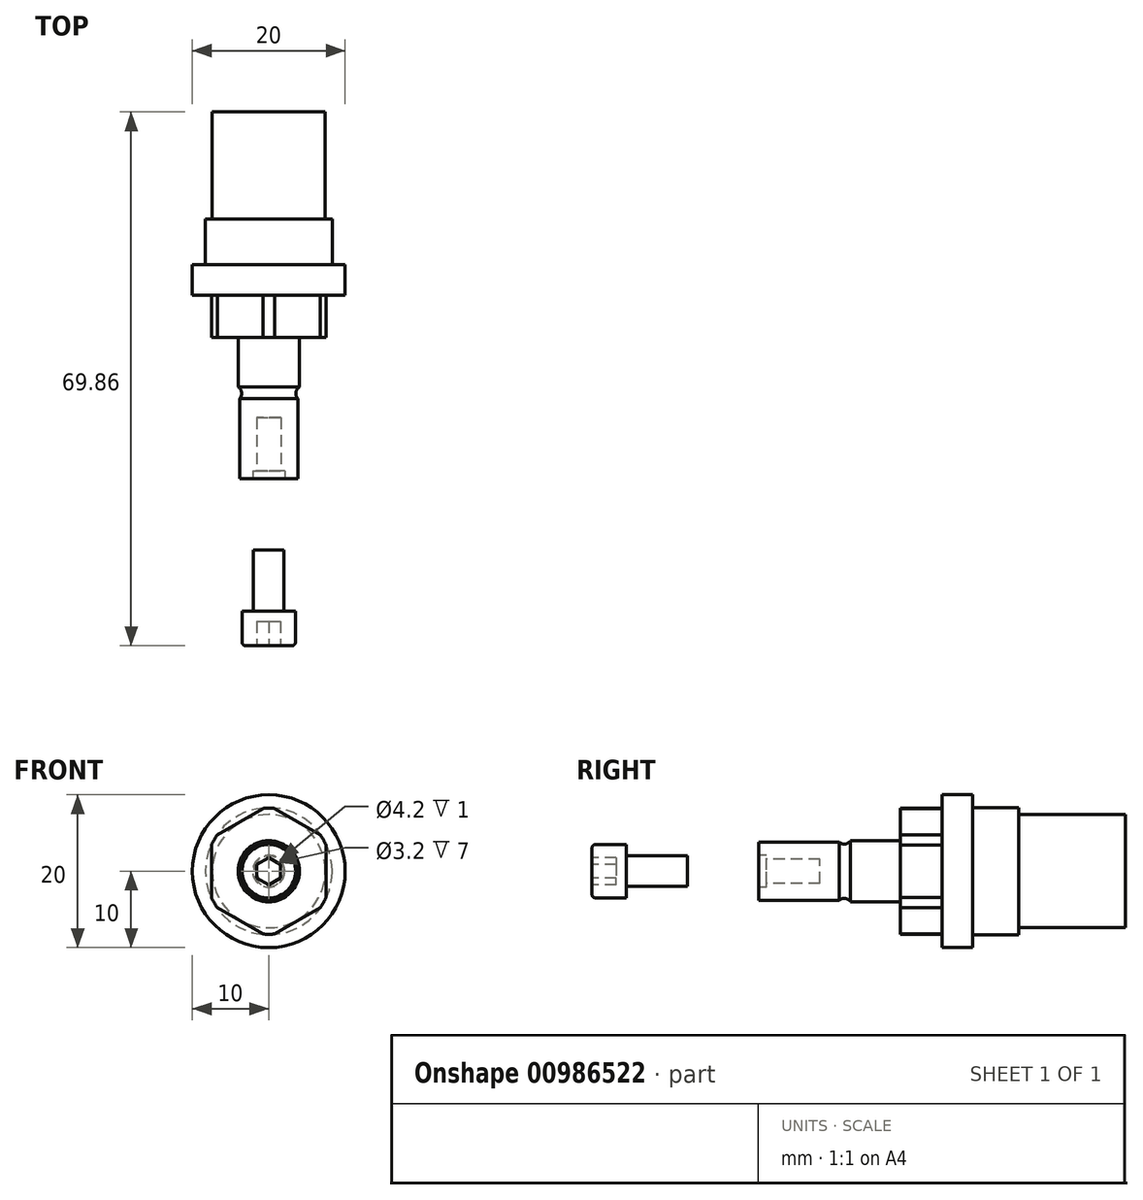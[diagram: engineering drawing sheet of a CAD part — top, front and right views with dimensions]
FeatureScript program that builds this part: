
annotation { "Feature Type Name" : "Feature", "Feature Type Description" : "" }
export const myFeature = defineFeature(function(context is Context, id is Id, definition is map)
    precondition{}
    {
        {
            var Q0;
            Q0=qCreatedBy(makeId("Right.planeOp"),FACE);
            var sketch = newSketch(context, id + "F0", { "sketchPlane" : qUnion([Q0])});
            skLineSegment(sketch, "E0", {"start": v(-42.4, 0) * mm, "end": v(45.83, 0) * mm, "construction": true});
            skLineSegment(sketch, "E1", {"start": v(20, 0) * mm, "end": v(20, 7.4) * mm});
            skLineSegment(sketch, "E2", {"start": v(20, 7.4) * mm, "end": v(6, 7.4) * mm});
            skLineSegment(sketch, "E3", {"start": v(6, 7.4) * mm, "end": v(6, 8.3) * mm});
            skLineSegment(sketch, "E4", {"start": v(6, 8.3) * mm, "end": v(0, 8.3) * mm});
            skLineSegment(sketch, "E5", {"start": v(0, 8.3) * mm, "end": v(0, 10) * mm});
            skLineSegment(sketch, "E6", {"start": v(0, 10) * mm, "end": v(-4, 10) * mm});
            skLineSegment(sketch, "E7", {"start": v(-4, 10) * mm, "end": v(-4, 8.25) * mm});
            skLineSegment(sketch, "E8", {"start": v(-4, 8.25) * mm, "end": v(-9.5, 8.25) * mm});
            skLineSegment(sketch, "E9", {"start": v(-9.5, 8.25) * mm, "end": v(-9.5, 4) * mm});
            skLineSegment(sketch, "E10", {"start": v(-9.5, 4) * mm, "end": v(-16, 4) * mm});
            skLineSegment(sketch, "E11", {"start": v(-17.5, 3.8) * mm, "end": v(-28, 3.8) * mm});
            skLineSegment(sketch, "E12", {"start": v(-28, 3.8) * mm, "end": v(-28, 2.1) * mm});
            skLineSegment(sketch, "E13", {"start": v(-28, 0) * mm, "end": v(20, 0) * mm});
            skArc(sketch, "E14", {"start": v(-17.5, 3.8) * mm, "mid": v(-16.7, 3.56) * mm, "end": v(-16, 4) * mm});
            skLineSegment(sketch, "E15", {"start": v(-28, 2.1) * mm, "end": v(-27, 2.1) * mm});
            skLineSegment(sketch, "E16", {"start": v(-27, 2.1) * mm, "end": v(-27, 1.6) * mm});
            skLineSegment(sketch, "E17", {"start": v(-27, 1.6) * mm, "end": v(-20, 1.6) * mm});
            skLineSegment(sketch, "E18", {"start": v(-20, 1.6) * mm, "end": v(-20, 0) * mm});
            skSolve(sketch);
        }
        {
            var Q0;
            Q0 = qSketchRegion(id + "F0", true);
            var Q1;
            Q1=sQuery(id+"F0.wireOp",EDGE,"E0");
            revolve(context, id + "F1", {"surfaceOperationType" : NewSurfaceOperationType.NEW, "entities" : qUnion([Q0]), "axis" : qUnion([Q1]), "revolveType" : RevolveType.FULL});
        }
        {
            var Q0;
            Q0=makeQuery(id+"F1.opRevolve","SWEPT_FACE",FACE,{"disambiguationData":[OSD([sQuery(id+"F0.wireOp",EDGE,"E9")])]});
            var sketch = newSketch(context, id + "F2", { "sketchPlane" : qUnion([Q0])});
            skCircle(sketch, "E19.cCircle", {"center": v(0, 0) * mm, "radius": 7.5 * mm, "construction": true});
            skLineSegment(sketch, "E19.0", {"start": v(7.5, 4.33) * mm, "end": v(7.5, -4.33) * mm});
            skLineSegment(sketch, "E19.1", {"start": v(7.5, -4.33) * mm, "end": v(0, -8.66) * mm});
            skLineSegment(sketch, "E19.2", {"start": v(0, -8.66) * mm, "end": v(-7.5, -4.33) * mm});
            skLineSegment(sketch, "E19.3", {"start": v(-7.5, -4.33) * mm, "end": v(-7.5, 4.33) * mm});
            skLineSegment(sketch, "E19.4", {"start": v(-7.5, 4.33) * mm, "end": v(0, 8.66) * mm});
            skLineSegment(sketch, "E19.5", {"start": v(0, 8.66) * mm, "end": v(7.5, 4.33) * mm});
            skPoint(sketch, "E19.0.midPoint", {"position": v(7.5, 0) * mm});
            skCircle(sketch, "E20.0", {"center": v(0, 0) * mm, "radius": 10 * mm});
            skSolve(sketch);
        }
        {
            var Q0;
            Q0 = qSketchRegion(id + "F2", true);
            var Q1;
            Q1=makeQuery(id+"F1.opRevolve","SWEPT_FACE",FACE,{"disambiguationData":[OSD([sQuery(id+"F0.wireOp",EDGE,"E7")])]});
            extrude(context, id + "F3", {"entities" : qUnion([Q0]), "operationType" : NewBodyOperationType.REMOVE, "endBound" : BoundingType.UP_TO_SURFACE, "oppositeDirection" : true, "depth" : 25 * mm, "endBoundEntityFace" : qUnion([Q1]), "offsetDistance" : 25 * mm});
        }
        {
            var Q0;
            Q0=qCreatedBy(makeId("Right.planeOp"),FACE);
            var sketch = newSketch(context, id + "F4", { "sketchPlane" : qUnion([Q0])});
            skLineSegment(sketch, "E21", {"start": v(-35.14, 0) * mm, "end": v(-55.4, 0) * mm, "construction": true});
            skLineSegment(sketch, "E22", {"start": v(-37.36, 0) * mm, "end": v(-37.36, 2) * mm});
            skLineSegment(sketch, "E23", {"start": v(-37.36, 2) * mm, "end": v(-45.36, 2) * mm});
            skLineSegment(sketch, "E24", {"start": v(-45.36, 2) * mm, "end": v(-45.36, 3.5) * mm});
            skLineSegment(sketch, "E25", {"start": v(-45.36, 3.5) * mm, "end": v(-49.36, 3.5) * mm});
            skLineSegment(sketch, "E26", {"start": v(-49.86, 3) * mm, "end": v(-49.86, 0) * mm});
            skLineSegment(sketch, "E27", {"start": v(-49.86, 0) * mm, "end": v(-37.36, 0) * mm});
            skPoint(sketch, "E28.visualSharp", {"position": v(-49.86, 3.5) * mm});
            skArc(sketch, "E28.filletArc", {"start": v(-49.36, 3.5) * mm, "mid": v(-49.71, 3.35) * mm, "end": v(-49.86, 3) * mm});
            skSolve(sketch);
        }
        {
            var Q0;
            Q0=makeQuery(id+"F4.imprint","IMPRINT",FACE,{"disambiguationData":[TD([[makeQuery(id+"F4.imprint","IMPRINT",EDGE,{"derivedFrom":sQuery(id+"F4.wireOp",EDGE,"E22")}),1.0]])]});
            var Q1;
            Q1=sQuery(id+"F4.wireOp",EDGE,"E21");
            revolve(context, id + "F5", {"surfaceOperationType" : NewSurfaceOperationType.NEW, "entities" : qUnion([Q0]), "axis" : qUnion([Q1]), "revolveType" : RevolveType.FULL});
        }
        {
            var Q0;
            Q0=makeQuery(id+"F5.opRevolve","SWEPT_FACE",FACE,{"disambiguationData":[OSD([sQuery(id+"F4.wireOp",EDGE,"E26")])]});
            var sketch = newSketch(context, id + "F6", { "sketchPlane" : qUnion([Q0])});
            skCircle(sketch, "E29.cCircle", {"center": v(0, 0) * mm, "radius": 1.55 * mm, "construction": true});
            skLineSegment(sketch, "E29.0", {"start": v(1.55, 0.9) * mm, "end": v(1.55, -0.9) * mm});
            skLineSegment(sketch, "E29.1", {"start": v(1.55, -0.9) * mm, "end": v(0, -1.79) * mm});
            skLineSegment(sketch, "E29.2", {"start": v(0, -1.79) * mm, "end": v(-1.55, -0.9) * mm});
            skLineSegment(sketch, "E29.3", {"start": v(-1.55, -0.9) * mm, "end": v(-1.55, 0.9) * mm});
            skLineSegment(sketch, "E29.4", {"start": v(-1.55, 0.9) * mm, "end": v(0, 1.79) * mm});
            skLineSegment(sketch, "E29.5", {"start": v(0, 1.79) * mm, "end": v(1.55, 0.9) * mm});
            skPoint(sketch, "E29.0.midPoint", {"position": v(1.55, 0) * mm});
            skSolve(sketch);
        }
        {
            var Q0;
            Q0 = qSketchRegion(id + "F6", true);
            extrude(context, id + "F7", {"entities" : qUnion([Q0]), "operationType" : NewBodyOperationType.REMOVE, "oppositeDirection" : true, "depth" : 3.2 * mm, "offsetDistance" : 25 * mm});
        }
    });
